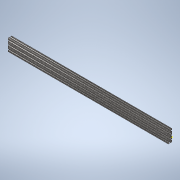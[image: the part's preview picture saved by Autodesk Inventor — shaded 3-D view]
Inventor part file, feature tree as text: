
AUTODESK INVENTOR PART (.ipt)
format: ipt  version: 2020 (Build 240168000, 168)  size: 400,896 bytes
history: native  units: in
note: dims shown in document units (in); Inventor stores cm internally (conversion verified against a paired STEP export)
features: sketch x2, extrude x1
ambient origin geometry x8: Origin, YZ Plane, XZ Plane, XY Plane, X Axis, Y Axis, Z Axis, Center Point
bodies: Solid1 (feature_tree)
feature tree (3):
  extrude  "Extrusion1"  [1 undecoded]
  sketch  "Sketch2"
  sketch  "Sketch1"  dims[d0=40.0in d1=0.0in]
note: 1 required parameter value undecoded (feature->parameter linkage not recoverable at this tier; creation-order binding heuristic only, values carry confidence <= 0.55)
